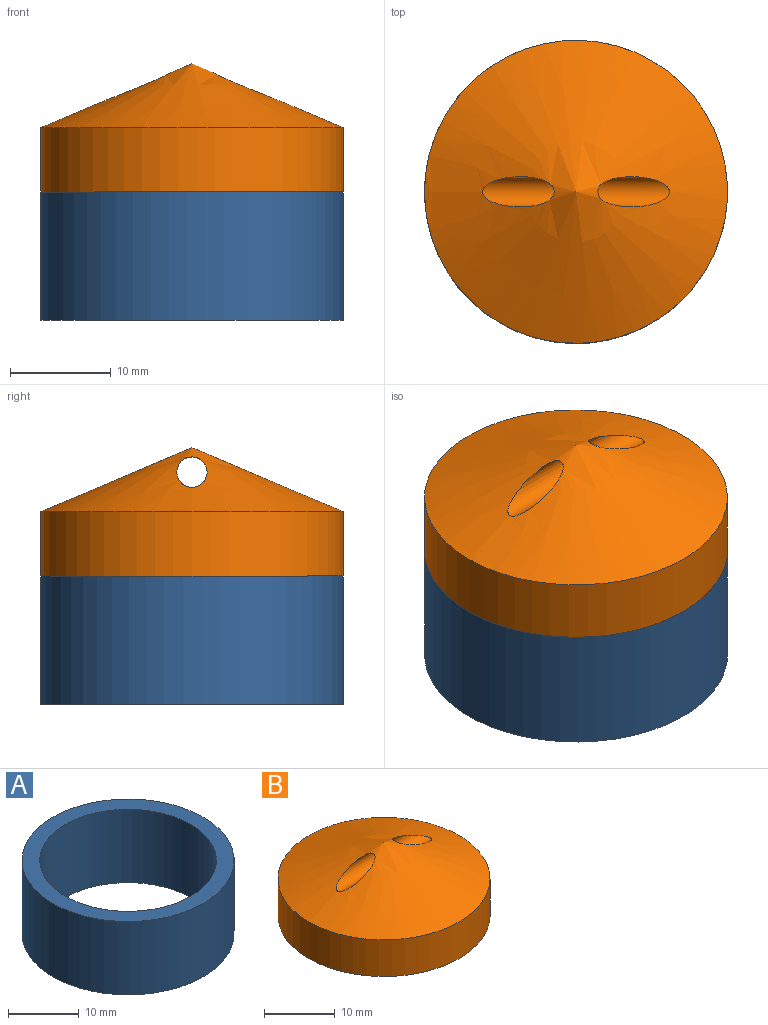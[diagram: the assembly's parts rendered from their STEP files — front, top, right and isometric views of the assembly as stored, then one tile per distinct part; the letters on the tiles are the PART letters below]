
ASSEMBLY  parts=2 mates=1
PART A: 4 faces, bbox 30x30x12.7 mm
  f0: cylinder r=12.5mm len=25mm, axis (0,0,-1), area 997.5mm2, adj f2,f3
  f1: cylinder r=15mm len=30mm, axis (0,0,-1), area 1196.9mm2, adj f2,f3
  f2: plane 30x30mm, normal (0,0,1), area 216mm2, adj f0,f1
  f3: plane 30x30mm, normal (0,0,-1), area 216mm2, adj f0,f1
PART B: 4 faces, bbox 30x30x12.7 mm
  f0: cone r=15mm half-angle=67.1deg, axis (0,0,-1), area 730.9mm2, adj f1,f3
  f1: cylinder r=15mm len=30mm, axis (0,0,1), area 598.5mm2, adj f0,f2
  f2: plane 30x30mm, normal (0,0,-1), area 706.9mm2, adj f1
  f3: cylinder r=1.5mm len=18.5mm, axis (1,0,0), area 105.4mm2, adj f0
PLACE A rot(axis=(-0.17,-0.91,-0.37),0deg) t=(-1.57,19.87,5.87)mm
PLACE B rot(axis=(-0.17,-0.91,-0.37),0deg) t=(-1.57,19.87,24.92)mm
MATE fastened A.f1 <-> B.f0  axis (0,0,1) through (-1.57,19.87,18.57)mm
